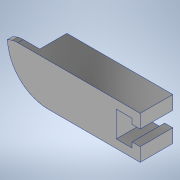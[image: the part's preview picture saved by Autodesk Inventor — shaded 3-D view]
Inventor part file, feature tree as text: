
AUTODESK INVENTOR PART (.ipt)
format: ipt  version: 2022 (Build 260153000, 153)  size: 162,816 bytes
history: native  units: mm
features: extrude x3, sketch x3, fillet x1
ambient origin geometry x8: Origin, YZ Plane, XZ Plane, XY Plane, X Axis, Y Axis, Z Axis, Center Point
bodies: Body1 (feature_tree)
feature tree (7):
  extrude  "Extrusion2"  Depth=5.8mm
  extrude  "Extrusion7"  Depth=12.0mm TaperAngle=0.0deg
  extrude  "Extrusion10"  Depth=15.6mm
  fillet  "Fillet2"  [1 undecoded]
  sketch  "Sketch5"  dims[d41=5.8mm d48=44.0mm]
  sketch  "Sketch11"  dims[d50=3.0mm d56=12.0mm d57=0.0mm]
  sketch  "Sketch14"  dims[d63=45.0mm d67=15.6mm d71=0.0mm d72=36.2mm d87=5.6mm d88=9.5mm d95=17.453293mm d96=8.0mm d97=15.0mm d98=10.0mm d99=0.0mm d108=0.0mm d109=0.0mm d110=15.0mm d111=10.0mm]
note: 1 required parameter value undecoded (feature->parameter linkage not recoverable at this tier; creation-order binding heuristic only, values carry confidence <= 0.55)
